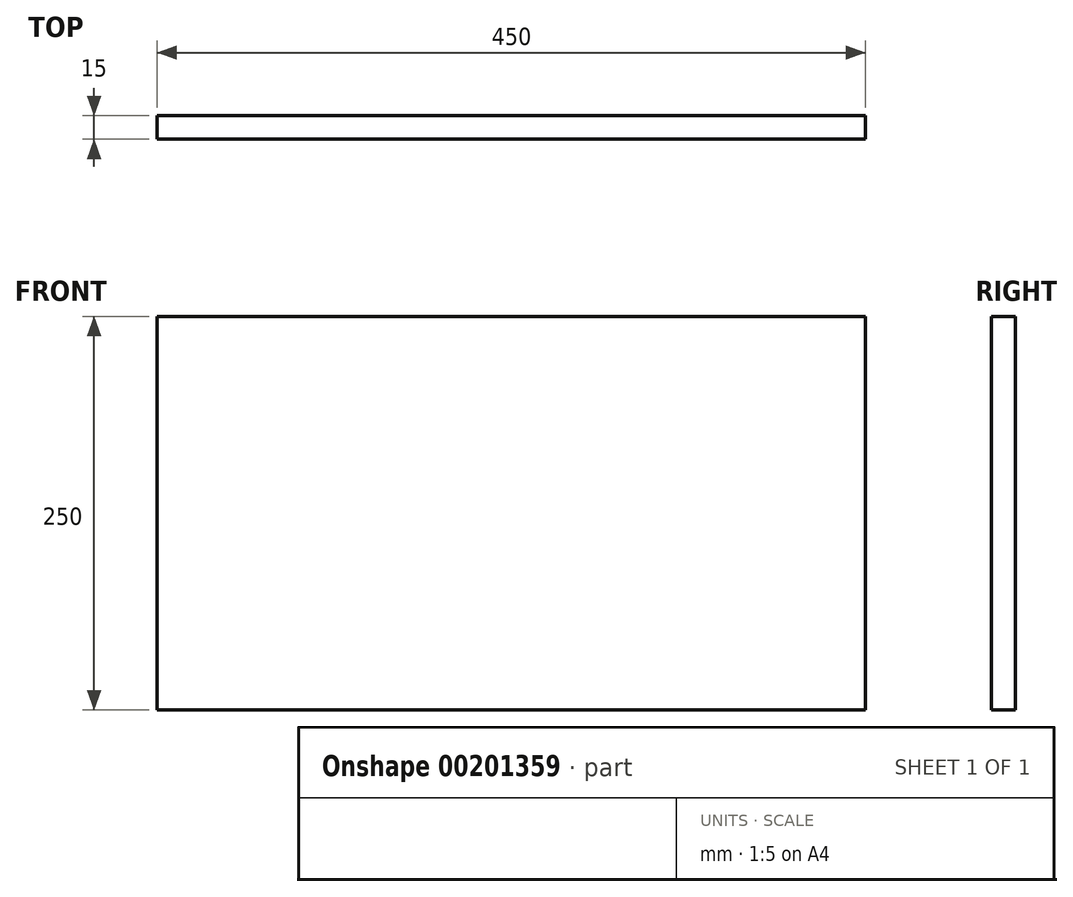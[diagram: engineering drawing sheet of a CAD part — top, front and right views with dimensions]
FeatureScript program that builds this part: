
annotation { "Feature Type Name" : "Feature", "Feature Type Description" : "" }
export const myFeature = defineFeature(function(context is Context, id is Id, definition is map)
    precondition{}
    {
        {
            var Q0;
            Q0=qCreatedBy(makeId("Front.planeOp"),FACE);
            var sketch = newSketch(context, id + "F0", { "sketchPlane" : qUnion([Q0])});
            skLineSegment(sketch, "E0.bottom", {"start": v(-225, 125) * mm, "end": v(225, 125) * mm});
            skLineSegment(sketch, "E0.top", {"start": v(-225, -125) * mm, "end": v(225, -125) * mm});
            skLineSegment(sketch, "E0.left", {"start": v(-225, 125) * mm, "end": v(-225, -125) * mm});
            skLineSegment(sketch, "E0.right", {"start": v(225, 125) * mm, "end": v(225, -125) * mm});
            skLineSegment(sketch, "E1", {"start": v(-386.61, 0) * mm, "end": v(346.51, 0) * mm, "construction": true});
            skLineSegment(sketch, "E2", {"start": v(0, 298.85) * mm, "end": v(0, -198.3) * mm, "construction": true});
            skSolve(sketch);
        }
        {
            var Q0;
            Q0 = qSketchRegion(id + "F0", true);
            extrude(context, id + "F1", {"entities" : qUnion([Q0]), "depth" : 15 * mm});
        }
    });
